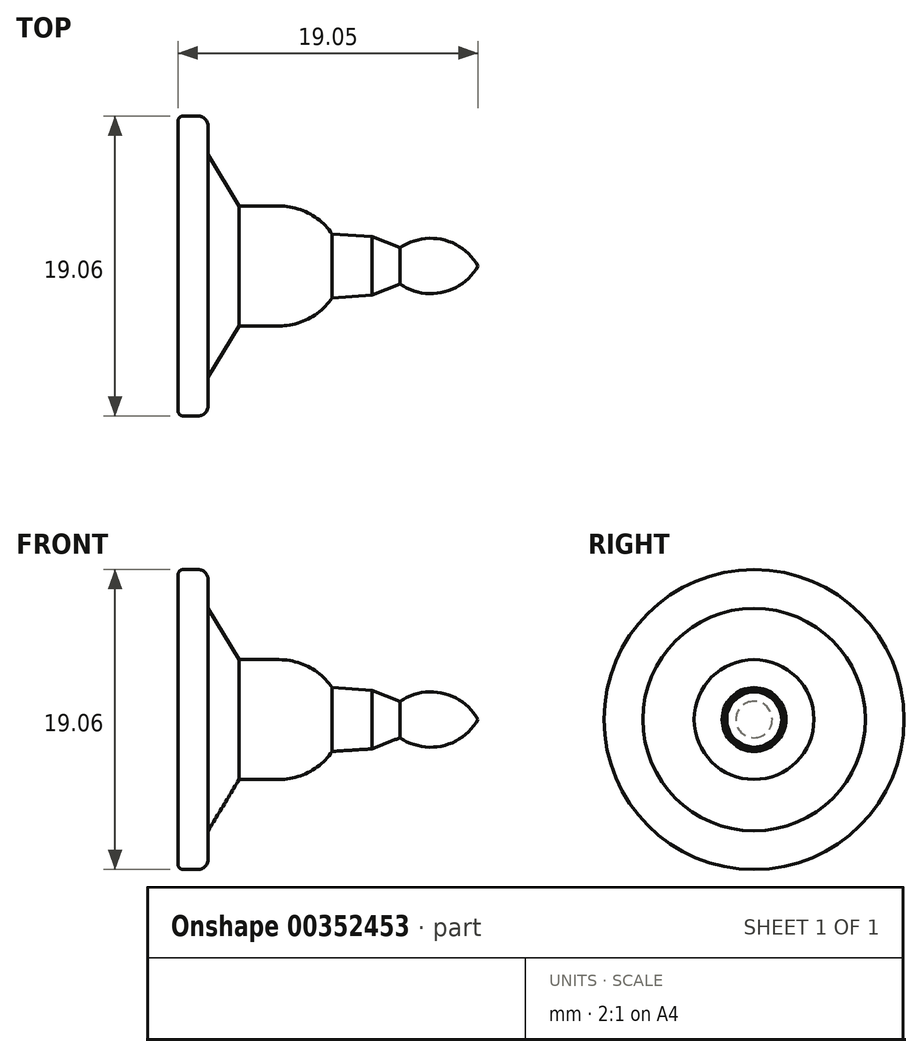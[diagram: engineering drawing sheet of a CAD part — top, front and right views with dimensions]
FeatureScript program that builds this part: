
annotation { "Feature Type Name" : "Feature", "Feature Type Description" : "" }
export const myFeature = defineFeature(function(context is Context, id is Id, definition is map)
    precondition{}
    {
        {
            var Q0;
            Q0=qCreatedBy(makeId("Front.planeOp"),FACE);
            var sketch = newSketch(context, id + "F0", { "sketchPlane" : qUnion([Q0])});
            skLineSegment(sketch, "E0", {"start": v(0, 0) * mm, "end": v(-19.05, 0) * mm});
            skLineSegment(sketch, "E1", {"start": v(-19.05, 0) * mm, "end": v(-19.05, 9.52) * mm});
            skLineSegment(sketch, "E2", {"start": v(-19.05, 9.52) * mm, "end": v(-17.15, 9.52) * mm});
            skLineSegment(sketch, "E3", {"start": v(-17.15, 9.52) * mm, "end": v(-17.15, 7.06) * mm});
            skLineSegment(sketch, "E4", {"start": v(-15.17, 3.8) * mm, "end": v(-12.63, 3.8) * mm});
            skLineSegment(sketch, "E5", {"start": v(-6.73, 1.86) * mm, "end": v(-4.96, 1.15) * mm});
            skArc(sketch, "E6", {"start": v(0, 0) * mm, "mid": v(-2.23, 1.67) * mm, "end": v(-4.96, 1.15) * mm});
            skLineSegment(sketch, "E7", {"start": v(-9.26, 2.03) * mm, "end": v(-6.73, 1.86) * mm});
            skLineSegment(sketch, "E8", {"start": v(-17.15, 7.06) * mm, "end": v(-15.17, 3.8) * mm});
            skArc(sketch, "E9", {"start": v(-9.26, 2.03) * mm, "mid": v(-10.73, 3.33) * mm, "end": v(-12.63, 3.8) * mm});
            skSolve(sketch);
        }
        {
            var Q0;
            Q0=makeQuery(id+"F0.imprint","IMPRINT",FACE,{"disambiguationData":[TD([[makeQuery(id+"F0.imprint","IMPRINT",EDGE,{"derivedFrom":sQuery(id+"F0.wireOp",EDGE,"E0")}),-1.0]])]});
            var Q1;
            Q1=sQuery(id+"F0.wireOp",EDGE,"E0");
            revolve(context, id + "F1", {"entities" : qUnion([Q0]), "axis" : qUnion([Q1]), "revolveType" : RevolveType.FULL});
        }
        {
            var Q0;
            Q0=makeQuery(id+"F1.opRevolve","SWEPT_EDGE",EDGE,{"disambiguationData":[OSD([sQuery(id+"F0.wireOp",EDGE,"E2"),sQuery(id+"F0.wireOp",EDGE,"E3")])]});
            fillet(context, id + "F2", {"entities" : qUnion([Q0]), "radius" : 0.64 * mm, "tangentPropagation" : true, "allowEdgeOverflow" : false});
        }
        {
            var Q0;
            Q0=makeQuery(id+"F1.opRevolve","SWEPT_EDGE",EDGE,{"disambiguationData":[OSD([sQuery(id+"F0.wireOp",EDGE,"E1"),sQuery(id+"F0.wireOp",EDGE,"E2")])]});
            fillet(context, id + "F3", {"entities" : qUnion([Q0]), "radius" : 0.32 * mm, "tangentPropagation" : true, "allowEdgeOverflow" : false});
        }
    });
